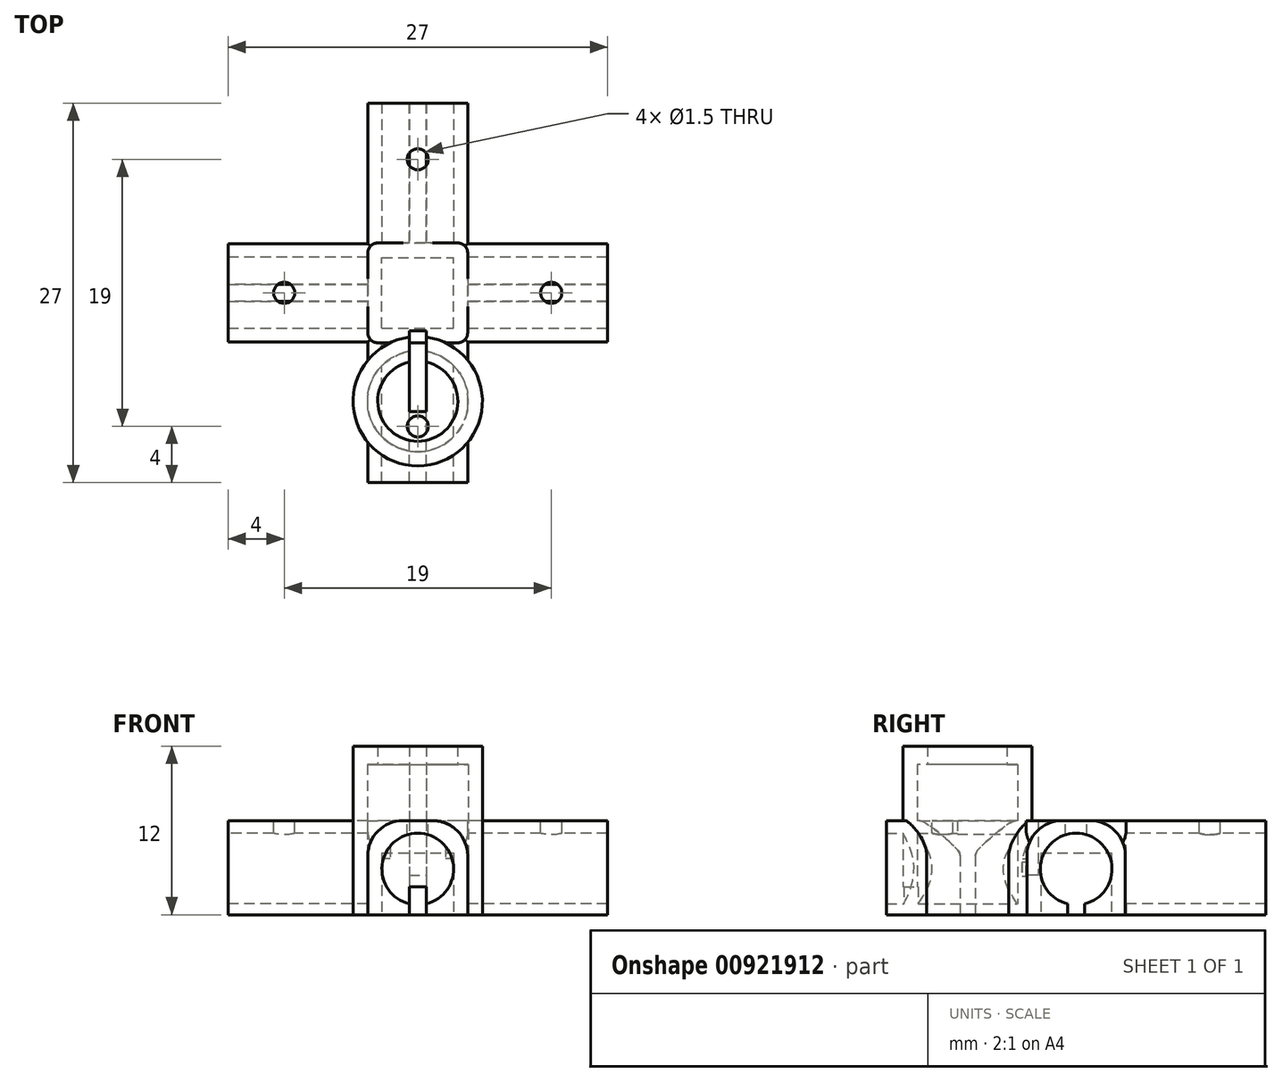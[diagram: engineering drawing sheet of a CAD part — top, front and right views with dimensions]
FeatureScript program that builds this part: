
annotation { "Feature Type Name" : "Feature", "Feature Type Description" : "" }
export const myFeature = defineFeature(function(context is Context, id is Id, definition is map)
    precondition{}
    {
        {
            var Q0;
            Q0=qCreatedBy(makeId("Front.planeOp"),FACE);
            var sketch = newSketch(context, id + "F0", { "sketchPlane" : qUnion([Q0])});
            skLineSegment(sketch, "E0.bottom", {"start": v(-3.55, 0) * mm, "end": v(3.55, 0) * mm});
            skLineSegment(sketch, "E0.top", {"start": v(-0.55, 6.7) * mm, "end": v(0.55, 6.7) * mm});
            skLineSegment(sketch, "E0.left", {"start": v(-3.55, 0) * mm, "end": v(-3.55, 3.7) * mm});
            skLineSegment(sketch, "E0.right", {"start": v(3.55, 0) * mm, "end": v(3.55, 3.7) * mm});
            skPoint(sketch, "E1.visualSharp", {"position": v(-3.55, 6.7) * mm});
            skArc(sketch, "E1.filletArc", {"start": v(-0.55, 6.7) * mm, "mid": v(-2.67, 5.82) * mm, "end": v(-3.55, 3.7) * mm});
            skPoint(sketch, "E2.visualSharp", {"position": v(3.55, 6.7) * mm});
            skArc(sketch, "E2.filletArc", {"start": v(3.55, 3.7) * mm, "mid": v(2.67, 5.82) * mm, "end": v(0.55, 6.7) * mm});
            skCircle(sketch, "E3", {"center": v(0, 3.25) * mm, "radius": 2.55 * mm});
            skSolve(sketch);
        }
        {
            var Q0;
            Q0 = qSketchRegion(id + "F0", true);
            extrude(context, id + "F1", {"entities" : qUnion([Q0]), "oppositeDirection" : true, "depth" : 9 * mm, "offsetDistance" : 25 * mm});
        }
        {
            var Q0;
            Q0=makeQuery(id+"F1.opExtrude","CAP_FACE",FACE,{"disambiguationData":[OSD([sQuery(id+"F0.wireOp",EDGE,"chtUnYgL-5RlG-UBpc-Dsll-1biOOoxe9lEl"),sQuery(id+"F0.wireOp",EDGE,"E0.bottom"),sQuery(id+"F0.wireOp",EDGE,"E0.top"),sQuery(id+"F0.wireOp",EDGE,"E0.left"),sQuery(id+"F0.wireOp",EDGE,"E0.right"),sQuery(id+"F0.wireOp",EDGE,"E1.filletArc"),sQuery(id+"F0.wireOp",EDGE,"E2.filletArc")])],"isStart":true});
            var sketch = newSketch(context, id + "F2", { "sketchPlane" : qUnion([Q0])});
            skLineSegment(sketch, "E4.0", {"start": v(-3.55, 0) * mm, "end": v(-3.55, 3.7) * mm});
            skLineSegment(sketch, "E4.1", {"start": v(3.55, 0) * mm, "end": v(3.55, 3.7) * mm});
            skArc(sketch, "E4.2", {"start": v(3.55, 3.7) * mm, "mid": v(2.67, 5.82) * mm, "end": v(0.55, 6.7) * mm});
            skLineSegment(sketch, "E4.3", {"start": v(-3.55, 0) * mm, "end": v(3.55, 0) * mm});
            skLineSegment(sketch, "E4.4", {"start": v(-0.55, 6.7) * mm, "end": v(0.55, 6.7) * mm});
            skArc(sketch, "E4.5", {"start": v(-0.55, 6.7) * mm, "mid": v(-2.67, 5.82) * mm, "end": v(-3.55, 3.7) * mm});
            skSolve(sketch);
        }
        {
            var Q0;
            Q0 = qSketchRegion(id + "F2", true);
            extrude(context, id + "F3", {"entities" : qUnion([Q0]), "operationType" : NewBodyOperationType.ADD, "depth" : 0.7 * mm, "offsetDistance" : 25 * mm});
        }
        {
            var Q0;
            Q0=makeQuery(id+"F3.opExtrude","CAP_FACE",FACE,{"disambiguationData":[OSD([sQuery(id+"F2.wireOp",EDGE,"E4.0"),sQuery(id+"F2.wireOp",EDGE,"E4.1"),sQuery(id+"F2.wireOp",EDGE,"E4.2"),sQuery(id+"F2.wireOp",EDGE,"E4.3"),sQuery(id+"F2.wireOp",EDGE,"E4.4"),sQuery(id+"F2.wireOp",EDGE,"E4.5")])],"isStart":false});
            var sketch = newSketch(context, id + "F4", { "sketchPlane" : qUnion([Q0])});
            skLineSegment(sketch, "E5.bottom", {"start": v(-2.5, 4) * mm, "end": v(2.5, 4) * mm});
            skLineSegment(sketch, "E5.top", {"start": v(-2.5, 0) * mm, "end": v(2.5, 0) * mm});
            skLineSegment(sketch, "E5.left", {"start": v(-2.5, 4) * mm, "end": v(-2.5, 0) * mm});
            skLineSegment(sketch, "E5.right", {"start": v(2.5, 4) * mm, "end": v(2.5, 0) * mm});
            skSolve(sketch);
        }
        {
            var Q0;
            Q0 = qSketchRegion(id + "F4", true);
            extrude(context, id + "F5", {"entities" : qUnion([Q0]), "operationType" : NewBodyOperationType.ADD, "depth" : 3.15 * mm, "offsetDistance" : 25 * mm});
        }
        {
            var Q0;
            Q0=qCreatedBy(makeId("Top.planeOp"),FACE);
            var sketch = newSketch(context, id + "F6", { "sketchPlane" : qUnion([Q0])});
            skCircle(sketch, "E6", {"center": v(0, -7.71) * mm, "radius": 3.59 * mm});
            skCircle(sketch, "E7", {"center": v(0, -7.71) * mm, "radius": 4.6 * mm});
            skSolve(sketch);
        }
        {
            var Q0;
            Q0 = qSketchRegion(id + "F6", true);
            extrude(context, id + "F7", {"entities" : qUnion([Q0]), "operationType" : NewBodyOperationType.ADD, "depth" : 11 * mm, "offsetDistance" : 25 * mm});
        }
        {
            var Q0;
            Q0=makeQuery(id+"F7.opExtrude","CAP_FACE",FACE,{"disambiguationData":[OSD([sQuery(id+"F6.wireOp",EDGE,"E6"),sQuery(id+"F6.wireOp",EDGE,"E7")])],"isStart":false});
            var sketch = newSketch(context, id + "F8", { "sketchPlane" : qUnion([Q0])});
            skCircle(sketch, "E8", {"center": v(0, -7.71) * mm, "radius": 4.6 * mm});
            skCircle(sketch, "E9", {"center": v(0, -7.71) * mm, "radius": 2.85 * mm});
            skSolve(sketch);
        }
        {
            var Q0;
            Q0 = qSketchRegion(id + "F8", true);
            extrude(context, id + "F9", {"entities" : qUnion([Q0]), "operationType" : NewBodyOperationType.ADD, "depth" : 1 * mm, "offsetDistance" : 25 * mm, "hasSecondDirection" : true, "secondDirectionOppositeDirection" : true, "secondDirectionDepth" : 0.3 * mm});
        }
        {
            var Q0;
            Q0=makeQuery(id+"F7.boolean.opBoolean","MERGE",FACE,{"derivedFrom":[makeQuery(id+"F5.boolean.opBoolean","MERGE",FACE,{"derivedFrom":[makeQuery(id+"F3.boolean.opBoolean","MERGE",FACE,{"derivedFrom":[makeQuery(id+"F1.opExtrude","SWEPT_FACE",FACE,{"disambiguationData":[OSD([sQuery(id+"F0.wireOp",EDGE,"E0.bottom")])]}),makeQuery(id+"F3.opExtrude","SWEPT_FACE",FACE,{"disambiguationData":[OSD([sQuery(id+"F2.wireOp",EDGE,"E4.3")])]})]}),makeQuery(id+"F5.opExtrude","SWEPT_FACE",FACE,{"disambiguationData":[OSD([sQuery(id+"F4.wireOp",EDGE,"E5.top")])]})]}),makeQuery(id+"F7.opExtrude","CAP_FACE",FACE,{"disambiguationData":[OSD([sQuery(id+"F6.wireOp",EDGE,"E6"),sQuery(id+"F6.wireOp",EDGE,"E7")])],"isStart":true})]});
            var sketch = newSketch(context, id + "F10", { "sketchPlane" : qUnion([Q0])});
            skLineSegment(sketch, "E10.bottom", {"start": v(0.6, 10.5) * mm, "end": v(-0.6, 10.5) * mm});
            skLineSegment(sketch, "E10.top", {"start": v(0.6, -10.5) * mm, "end": v(-0.6, -10.5) * mm});
            skLineSegment(sketch, "E10.left", {"start": v(0.6, 10.5) * mm, "end": v(0.6, -10.5) * mm});
            skLineSegment(sketch, "E10.right", {"start": v(-0.6, 10.5) * mm, "end": v(-0.6, -10.5) * mm});
            skSolve(sketch);
        }
        {
            var Q0;
            Q0 = qSketchRegion(id + "F10", true);
            extrude(context, id + "F11", {"entities" : qUnion([Q0]), "operationType" : NewBodyOperationType.REMOVE, "oppositeDirection" : true, "depth" : 2.8 * mm, "offsetDistance" : 25 * mm});
        }
        {
            var Q0;
            Q0=makeQuery(id+"F5.opExtrude","SWEPT_FACE",FACE,{"disambiguationData":[OSD([sQuery(id+"F4.wireOp",EDGE,"E5.bottom")])]});
            var sketch = newSketch(context, id + "F12", { "sketchPlane" : qUnion([Q0])});
            skLineSegment(sketch, "E11.bottom", {"start": v(-1.6, -2.71) * mm, "end": v(1.6, -2.71) * mm});
            skLineSegment(sketch, "E11.top", {"start": v(-1.6, -1.1) * mm, "end": v(1.6, -1.1) * mm});
            skLineSegment(sketch, "E11.left", {"start": v(-1.6, -2.71) * mm, "end": v(-1.6, -1.1) * mm});
            skLineSegment(sketch, "E11.right", {"start": v(1.6, -2.71) * mm, "end": v(1.6, -1.1) * mm});
            skSolve(sketch);
        }
        {
            var Q0;
            Q0 = qSketchRegion(id + "F12", true);
            extrude(context, id + "F13", {"entities" : qUnion([Q0]), "operationType" : NewBodyOperationType.REMOVE, "oppositeDirection" : true, "depth" : 25 * mm, "offsetDistance" : 25 * mm});
        }
        {
            var Q0;
            Q0=makeQuery(id+"F3.boolean.opBoolean","MERGE",FACE,{"derivedFrom":[makeQuery(id+"F1.opExtrude","SWEPT_FACE",FACE,{"disambiguationData":[OSD([sQuery(id+"F0.wireOp",EDGE,"E0.top")])]}),makeQuery(id+"F3.opExtrude","SWEPT_FACE",FACE,{"disambiguationData":[OSD([sQuery(id+"F2.wireOp",EDGE,"E4.4")])]})]});
            var sketch = newSketch(context, id + "F14", { "sketchPlane" : qUnion([Q0])});
            skCircle(sketch, "E12", {"center": v(0, 4) * mm, "radius": 0.75 * mm});
            skSolve(sketch);
        }
        {
            var Q0;
            Q0 = qSketchRegion(id + "F14", true);
            extrude(context, id + "F15", {"entities" : qUnion([Q0]), "operationType" : NewBodyOperationType.REMOVE, "oppositeDirection" : true, "depth" : 3 * mm, "offsetDistance" : 25 * mm});
        }
        {
            var Q0;
            Q0=qCreatedBy(makeId("Front.planeOp"),FACE);
            var sketch = newSketch(context, id + "F16", { "sketchPlane" : qUnion([Q0])});
            skLineSegment(sketch, "E13.bottom", {"start": v(-3.55, 0) * mm, "end": v(3.55, 0) * mm});
            skLineSegment(sketch, "E13.top", {"start": v(-1.05, 6.7) * mm, "end": v(1.05, 6.7) * mm});
            skLineSegment(sketch, "E13.left", {"start": v(-3.55, 0) * mm, "end": v(-3.55, 4.2) * mm});
            skLineSegment(sketch, "E13.right", {"start": v(3.55, 0) * mm, "end": v(3.55, 4.2) * mm});
            skPoint(sketch, "E14.visualSharp", {"position": v(3.55, 6.7) * mm});
            skArc(sketch, "E14.filletArc", {"start": v(3.55, 4.2) * mm, "mid": v(2.82, 5.97) * mm, "end": v(1.05, 6.7) * mm});
            skPoint(sketch, "E15.visualSharp", {"position": v(-3.55, 6.7) * mm});
            skArc(sketch, "E15.filletArc", {"start": v(-1.05, 6.7) * mm, "mid": v(-2.82, 5.97) * mm, "end": v(-3.55, 4.2) * mm});
            skCircle(sketch, "E16", {"center": v(0, 3.25) * mm, "radius": 2.55 * mm});
            skSolve(sketch);
        }
        {
            var Q0;
            Q0=qCreatedBy(makeId("Right.planeOp"),FACE);
            var sketch = newSketch(context, id + "F17", { "sketchPlane" : qUnion([Q0])});
            skLineSegment(sketch, "E17.bottom", {"start": v(1, 6.7) * mm, "end": v(-1, 6.7) * mm});
            skLineSegment(sketch, "E17.top", {"start": v(3.5, 0) * mm, "end": v(-3.5, 0) * mm});
            skLineSegment(sketch, "E17.left", {"start": v(3.5, 4.2) * mm, "end": v(3.5, 0) * mm});
            skLineSegment(sketch, "E17.right", {"start": v(-3.5, 4.2) * mm, "end": v(-3.5, 0) * mm});
            skPoint(sketch, "E18.visualSharp", {"position": v(3.5, 6.7) * mm});
            skArc(sketch, "E18.filletArc", {"start": v(3.5, 4.2) * mm, "mid": v(2.77, 5.97) * mm, "end": v(1, 6.7) * mm});
            skPoint(sketch, "E19.visualSharp", {"position": v(-3.5, 6.7) * mm});
            skArc(sketch, "E19.filletArc", {"start": v(-1, 6.7) * mm, "mid": v(-2.77, 5.97) * mm, "end": v(-3.5, 4.2) * mm});
            skCircle(sketch, "E20", {"center": v(0, 3.25) * mm, "radius": 2.55 * mm});
            skSolve(sketch);
        }
        {
            var Q0;
            Q0=makeQuery(id+"F17.imprint","IMPRINT",FACE,{"disambiguationData":[TD([[makeQuery(id+"F17.imprint","IMPRINT",EDGE,{"derivedFrom":sQuery(id+"F17.wireOp",EDGE,"E17.bottom")}),1.0]])]});
            extrude(context, id + "F18", {"entities" : qUnion([Q0]), "endBound" : BoundingType.SYMMETRIC, "depth" : 27 * mm, "offsetDistance" : 25 * mm});
        }
        {
            var Q0;
            Q0 = qSketchRegion(id + "F16", true);
            extrude(context, id + "F19", {"entities" : qUnion([Q0]), "operationType" : NewBodyOperationType.ADD, "endBound" : BoundingType.SYMMETRIC, "depth" : 27 * mm, "offsetDistance" : 25 * mm});
        }
        {
            var Q0;
            Q0=makeQuery(id+"F19.boolean.opBoolean","MERGE",FACE,{"derivedFrom":[makeQuery(id+"F18.opExtrude","SWEPT_FACE",FACE,{"disambiguationData":[OSD([sQuery(id+"F17.wireOp",EDGE,"E17.bottom")])]}),makeQuery(id+"F19.opExtrude","SWEPT_FACE",FACE,{"disambiguationData":[OSD([sQuery(id+"F16.wireOp",EDGE,"E13.top")])]})]});
            var sketch = newSketch(context, id + "F20", { "sketchPlane" : qUnion([Q0])});
            skLineSegment(sketch, "E21.bottom", {"start": v(3.55, 3.55) * mm, "end": v(-3.55, 3.55) * mm});
            skLineSegment(sketch, "E21.top", {"start": v(3.55, -3.55) * mm, "end": v(-3.55, -3.55) * mm});
            skLineSegment(sketch, "E21.left", {"start": v(3.55, 3.55) * mm, "end": v(3.55, -3.55) * mm});
            skLineSegment(sketch, "E21.right", {"start": v(-3.55, 3.55) * mm, "end": v(-3.55, -3.55) * mm});
            skSolve(sketch);
        }
        {
            var Q0;
            Q0=makeQuery(id+"F19.boolean.opBoolean","MERGE",FACE,{"derivedFrom":[makeQuery(id+"F18.opExtrude","SWEPT_FACE",FACE,{"disambiguationData":[OSD([sQuery(id+"F17.wireOp",EDGE,"E17.top")])]}),makeQuery(id+"F19.opExtrude","SWEPT_FACE",FACE,{"disambiguationData":[OSD([sQuery(id+"F16.wireOp",EDGE,"E13.bottom")])]})]});
            var sketch = newSketch(context, id + "F21", { "sketchPlane" : qUnion([Q0])});
            skLineSegment(sketch, "E22.bottom", {"start": v(-0.6, 13.5) * mm, "end": v(0.6, 13.5) * mm});
            skLineSegment(sketch, "E22.top", {"start": v(-0.6, -13.5) * mm, "end": v(0.6, -13.5) * mm});
            skLineSegment(sketch, "E22.left", {"start": v(-0.6, 13.5) * mm, "end": v(-0.6, 0.6) * mm});
            skLineSegment(sketch, "E22.right", {"start": v(0.6, 13.5) * mm, "end": v(0.6, 0.6) * mm});
            skLineSegment(sketch, "E23.bottom", {"start": v(-13.5, 0.6) * mm, "end": v(-0.6, 0.6) * mm});
            skLineSegment(sketch, "E23.top", {"start": v(-13.5, -0.6) * mm, "end": v(-0.6, -0.6) * mm});
            skLineSegment(sketch, "E23.left", {"start": v(-13.5, 0.6) * mm, "end": v(-13.5, -0.6) * mm});
            skLineSegment(sketch, "E23.right", {"start": v(13.5, 0.6) * mm, "end": v(13.5, -0.6) * mm});
            skLineSegment(sketch, "E24.trimOffspring", {"start": v(-0.6, -0.6) * mm, "end": v(-0.6, -13.5) * mm});
            skLineSegment(sketch, "E25.trimOffspring", {"start": v(0.6, -0.6) * mm, "end": v(0.6, -13.5) * mm});
            skLineSegment(sketch, "E26.trimOffspring", {"start": v(0.6, 0.6) * mm, "end": v(13.5, 0.6) * mm});
            skLineSegment(sketch, "E27.trimOffspring", {"start": v(0.6, -0.6) * mm, "end": v(13.5, -0.6) * mm});
            skSolve(sketch);
        }
        {
            var Q0;
            Q0 = qSketchRegion(id + "F21", true);
            extrude(context, id + "F22", {"entities" : qUnion([Q0]), "operationType" : NewBodyOperationType.REMOVE, "oppositeDirection" : true, "depth" : 2 * mm, "offsetDistance" : 25 * mm});
        }
        {
            var Q0;
            Q0 = qSketchRegion(id + "F20", true);
            var Q1;
            {var subQ1=sQuery(id+"F16.wireOp",EDGE,"E13.bottom");var subQ3=sQuery(id+"F17.wireOp",EDGE,"E17.top");Q1=makeQuery(id+"F22.boolean.opBoolean","SPLIT",FACE,{"disambiguationData":[TD([makeQuery(id+"F22.opExtrude","SWEPT_FACE",FACE,{"disambiguationData":[OSD([sQuery(id+"F21.wireOp",EDGE,"E22.left")])]})])],"derivedFrom":makeQuery(id+"F19.boolean.opBoolean","MERGE",FACE,{"derivedFrom":[makeQuery(id+"F18.opExtrude","SWEPT_FACE",FACE,{"disambiguationData":[OSD([subQ3])]}),makeQuery(id+"F19.opExtrude","SWEPT_FACE",FACE,{"disambiguationData":[OSD([subQ1])]})]})});}
            extrude(context, id + "F23", {"entities" : qUnion([Q0]), "operationType" : NewBodyOperationType.ADD, "endBound" : BoundingType.UP_TO_SURFACE, "oppositeDirection" : true, "depth" : 25 * mm, "endBoundEntityFace" : qUnion([Q1]), "offsetDistance" : 25 * mm});
        }
        {
            var Q0;
            Q0=makeQuery(id+"F23.opExtrude","SWEPT_EDGE",EDGE,{"disambiguationData":[OSD([sQuery(id+"F20.wireOp",EDGE,"E21.top"),sQuery(id+"F20.wireOp",EDGE,"E21.right")])]});
            var Q1;
            Q1=makeQuery(id+"F23.opExtrude","SWEPT_EDGE",EDGE,{"disambiguationData":[OSD([sQuery(id+"F20.wireOp",EDGE,"E21.top"),sQuery(id+"F20.wireOp",EDGE,"E21.left")])]});
            var Q2;
            Q2=makeQuery(id+"F23.opExtrude","SWEPT_EDGE",EDGE,{"disambiguationData":[OSD([sQuery(id+"F20.wireOp",EDGE,"E21.bottom"),sQuery(id+"F20.wireOp",EDGE,"E21.left")])]});
            var Q3;
            Q3=makeQuery(id+"F23.opExtrude","SWEPT_EDGE",EDGE,{"disambiguationData":[OSD([sQuery(id+"F20.wireOp",EDGE,"E21.bottom"),sQuery(id+"F20.wireOp",EDGE,"E21.right")])]});
            fillet(context, id + "F24", {"entities" : qUnion([Q0, Q1, Q2, Q3]), "radius" : 0.7 * mm, "tangentPropagation" : true, "allowEdgeOverflow" : false});
        }
        {
            var Q0;
            {var subQ6=sQuery(id+"F16.wireOp",EDGE,"E13.bottom");var subQ17=sQuery(id+"F17.wireOp",EDGE,"E17.top");var subQ20=makeQuery(id+"F19.boolean.opBoolean","MERGE",FACE,{"derivedFrom":[makeQuery(id+"F18.opExtrude","SWEPT_FACE",FACE,{"disambiguationData":[OSD([subQ17])]}),makeQuery(id+"F19.opExtrude","SWEPT_FACE",FACE,{"disambiguationData":[OSD([subQ6])]})]});Q0=makeQuery(id+"F23.boolean.opBoolean","MERGE",FACE,{"derivedFrom":[makeQuery(id+"F22.boolean.opBoolean","SPLIT",FACE,{"disambiguationData":[TD([makeQuery(id+"F22.opExtrude","SWEPT_FACE",FACE,{"disambiguationData":[OSD([sQuery(id+"F21.wireOp",EDGE,"E23.top")])]})])],"derivedFrom":subQ20}),makeQuery(id+"F22.boolean.opBoolean","SPLIT",FACE,{"disambiguationData":[TD([makeQuery(id+"F22.opExtrude","SWEPT_FACE",FACE,{"disambiguationData":[OSD([sQuery(id+"F21.wireOp",EDGE,"E25.trimOffspring")])]})])],"derivedFrom":subQ20}),makeQuery(id+"F22.boolean.opBoolean","SPLIT",FACE,{"disambiguationData":[TD([makeQuery(id+"F22.opExtrude","SWEPT_FACE",FACE,{"disambiguationData":[OSD([sQuery(id+"F21.wireOp",EDGE,"E22.left")])]})])],"derivedFrom":subQ20}),makeQuery(id+"F22.boolean.opBoolean","SPLIT",FACE,{"disambiguationData":[TD([makeQuery(id+"F22.opExtrude","SWEPT_FACE",FACE,{"disambiguationData":[OSD([sQuery(id+"F21.wireOp",EDGE,"E22.right")])]})])],"derivedFrom":subQ20}),makeQuery(id+"F23.opExtrude","CAP_FACE",FACE,{"disambiguationData":[OSD([sQuery(id+"F20.wireOp",EDGE,"E21.bottom"),sQuery(id+"F20.wireOp",EDGE,"E21.top"),sQuery(id+"F20.wireOp",EDGE,"E21.left"),sQuery(id+"F20.wireOp",EDGE,"E21.right")])],"isStart":false})]});}
            var sketch = newSketch(context, id + "F25", { "sketchPlane" : qUnion([Q0])});
            skLineSegment(sketch, "E28.bottom", {"start": v(-2.55, 2.5) * mm, "end": v(2.55, 2.5) * mm});
            skLineSegment(sketch, "E28.top", {"start": v(-2.55, -2.5) * mm, "end": v(2.55, -2.5) * mm});
            skLineSegment(sketch, "E28.left", {"start": v(-2.55, 2.5) * mm, "end": v(-2.55, -2.5) * mm});
            skLineSegment(sketch, "E28.right", {"start": v(2.55, 2.5) * mm, "end": v(2.55, -2.5) * mm});
            skSolve(sketch);
        }
        {
            var Q0;
            Q0 = qSketchRegion(id + "F25", true);
            extrude(context, id + "F26", {"entities" : qUnion([Q0]), "operationType" : NewBodyOperationType.REMOVE, "oppositeDirection" : true, "depth" : 4.4 * mm, "offsetDistance" : 25 * mm});
        }
        {
            var Q0;
            Q0=makeQuery(id+"F23.boolean.opBoolean","MERGE",FACE,{"derivedFrom":[makeQuery(id+"F19.boolean.opBoolean","MERGE",FACE,{"derivedFrom":[makeQuery(id+"F18.opExtrude","SWEPT_FACE",FACE,{"disambiguationData":[OSD([sQuery(id+"F17.wireOp",EDGE,"E17.bottom")])]}),makeQuery(id+"F19.opExtrude","SWEPT_FACE",FACE,{"disambiguationData":[OSD([sQuery(id+"F16.wireOp",EDGE,"E13.top")])]})]}),makeQuery(id+"F23.opExtrude","CAP_FACE",FACE,{"disambiguationData":[OSD([sQuery(id+"F20.wireOp",EDGE,"E21.bottom"),sQuery(id+"F20.wireOp",EDGE,"E21.top"),sQuery(id+"F20.wireOp",EDGE,"E21.left"),sQuery(id+"F20.wireOp",EDGE,"E21.right")])],"isStart":true})]});
            var sketch = newSketch(context, id + "F27", { "sketchPlane" : qUnion([Q0])});
            skCircle(sketch, "E29", {"center": v(9.5, 0) * mm, "radius": 0.75 * mm});
            skCircle(sketch, "E30", {"center": v(0, 9.5) * mm, "radius": 0.75 * mm});
            skCircle(sketch, "E31.MirrorC", {"center": v(0, -9.5) * mm, "radius": 0.75 * mm});
            skCircle(sketch, "E32.MirrorC", {"center": v(-9.5, 0) * mm, "radius": 0.75 * mm});
            skSolve(sketch);
        }
        {
            var Q0;
            Q0 = qSketchRegion(id + "F27", true);
            extrude(context, id + "F28", {"entities" : qUnion([Q0]), "operationType" : NewBodyOperationType.REMOVE, "oppositeDirection" : true, "depth" : 2 * mm, "offsetDistance" : 25 * mm});
        }
        {
            var Q0;
            {var subQ0=sQuery(id+"F10.wireOp",EDGE,"E10.left");var subQ1=sQuery(id+"F10.wireOp",EDGE,"E10.right");Q0=makeQuery(id+"F13.boolean.opBoolean","SPLIT",FACE,{"disambiguationData":[TD([makeQuery(id+"F7.opExtrude","SWEPT_FACE",FACE,{"disambiguationData":[OSD([sQuery(id+"F6.wireOp",EDGE,"E6")])]})])],"derivedFrom":makeQuery(id+"F11.boolean.opBoolean","COPY",FACE,{"derivedFrom":makeQuery(id+"F11.opExtrude","CAP_FACE",FACE,{"disambiguationData":[OSD([sQuery(id+"F10.wireOp",EDGE,"E10.bottom"),sQuery(id+"F10.wireOp",EDGE,"E10.top"),subQ0,subQ1])],"isStart":false})})});}
            var sketch = newSketch(context, id + "F29", { "sketchPlane" : qUnion([Q0])});
            skLineSegment(sketch, "E33.bottom", {"start": v(-0.6, 2.71) * mm, "end": v(0.6, 2.71) * mm});
            skLineSegment(sketch, "E33.top", {"start": v(-0.6, 8.46) * mm, "end": v(0.6, 8.46) * mm});
            skLineSegment(sketch, "E33.left", {"start": v(-0.6, 2.71) * mm, "end": v(-0.6, 8.46) * mm});
            skLineSegment(sketch, "E33.right", {"start": v(0.6, 2.71) * mm, "end": v(0.6, 8.46) * mm});
            skSolve(sketch);
        }
        {
            var Q0;
            Q0 = qSketchRegion(id + "F29", true);
            extrude(context, id + "F30", {"entities" : qUnion([Q0]), "operationType" : NewBodyOperationType.REMOVE, "oppositeDirection" : true, "depth" : 25 * mm, "offsetDistance" : 25 * mm});
        }
    });
